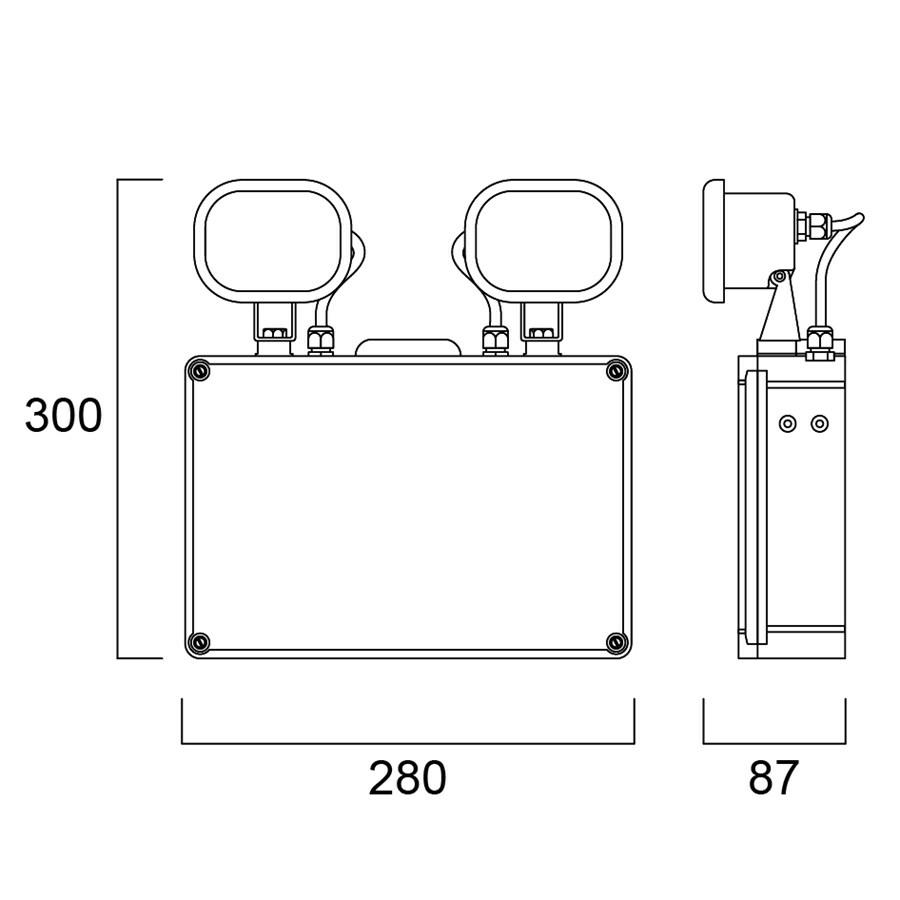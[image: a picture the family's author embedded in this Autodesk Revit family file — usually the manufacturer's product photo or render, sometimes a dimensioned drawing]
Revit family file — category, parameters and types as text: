
# Revit family: 0041769
name_source: partatom
category: Lighting Fixtures
revit_build: Autodesk Revit 2017 (Build: 20160225_1515(x64)
units: mm (PartAtom-declared; Revit-internal decimal feet)

## family parameters
Cut with Voids When Loaded = No
Host = Face
Light Source = No
OmniClass Number = 23.80.70.00
OmniClass Title = Lighting
Part Type = Normal
Room Calculation Point = No
Round Connector Dimension = Use Diameter
Shared = No

## types (1)
- 0041769 SYLSAFE TWIN TS C EM3 NM MS
    Apparent Load = 3 VA
    Assembly Code = D5020200
    AssetType = Fixed
    ClassificationName = Uniclass2015
    ClassificationValue = EF_70_80
    Cost = 0 $
    Default Elevation = 1219 mm
    Description = SylSafe Twin TS C EM3 NM MS is a dust and waterproof wall mounted twin LED projector for industrial applications. Two individually adjustable heads each delivering 200Lm. White housing colour. Non-maintained 3hr emergency operation with NiCd rechargeable battery. Recharge period 24 hours. 400Lm, 3.23W, IK03, IP65, Power Factor 0.6. Class I electrical construction.
    DocumentationLiterature = http://www.sylvania-lighting.com
    ElectricShockClassification = Class I
    IfcExportAs = IfcLightFixtureType
    IfcExportType = IfcLightFixtureType
    ImpactProtectionIndex = IK03
    IngressProtection = IP65
    InputNominalFrequency = 50/60 Hz
    Keynote = 16500
    Lamp = LED
    LampColourRenderingIndex = 70
    LampColourTemperature = 5700 K
    LampNominalLuminous = 400 lm
    LampsType = LED
    LuminousEfficacy = 124 lm/W
    Manufacturer = Feilo Sylvania
    ManufacturerName = Feilo Sylvania
    Material_1_SYL = PC/ABS Plastic
    Material_2_SYL = Aluminum
    Material_3_SYL = <By Category>
    Material_4_SYL = <By Category>
    Model = SylSafe Twin TS C EM3 NM MS
    ModelNumber = 0041769
    ModelReference = SylSafe Twin TS C EM3 NM MS
    Name = SylSafe Twin TS C EM3 NM MS
    NominalDepth = 87 mm
    NominalHeight = 300 mm
    NominalLength = 280 mm  [stored 0.918635 ft]
    PowerConsumption = 3.23 W
    PowerFactor = 0.6
    Type Image = <None>
    TypeLampHead_SYL = sylsafe_twin_lamp_head : 0041769 SYLSAFE TWIN TS C EM3 NM MS
    TypeName = SylSafe Twin TS C EM3 NM MS
    URL = http://www.sylvania-lighting.com
    Voltage = 220 V
    Weight = 8.5 kg

note: [stored X ft] marks values corroborated as IEEE doubles in the binary element streams (Revit-internal decimal feet)

## geometry (parser evidence)
native form markers: Sweep x2
no freeform markers — native parametric forms only
